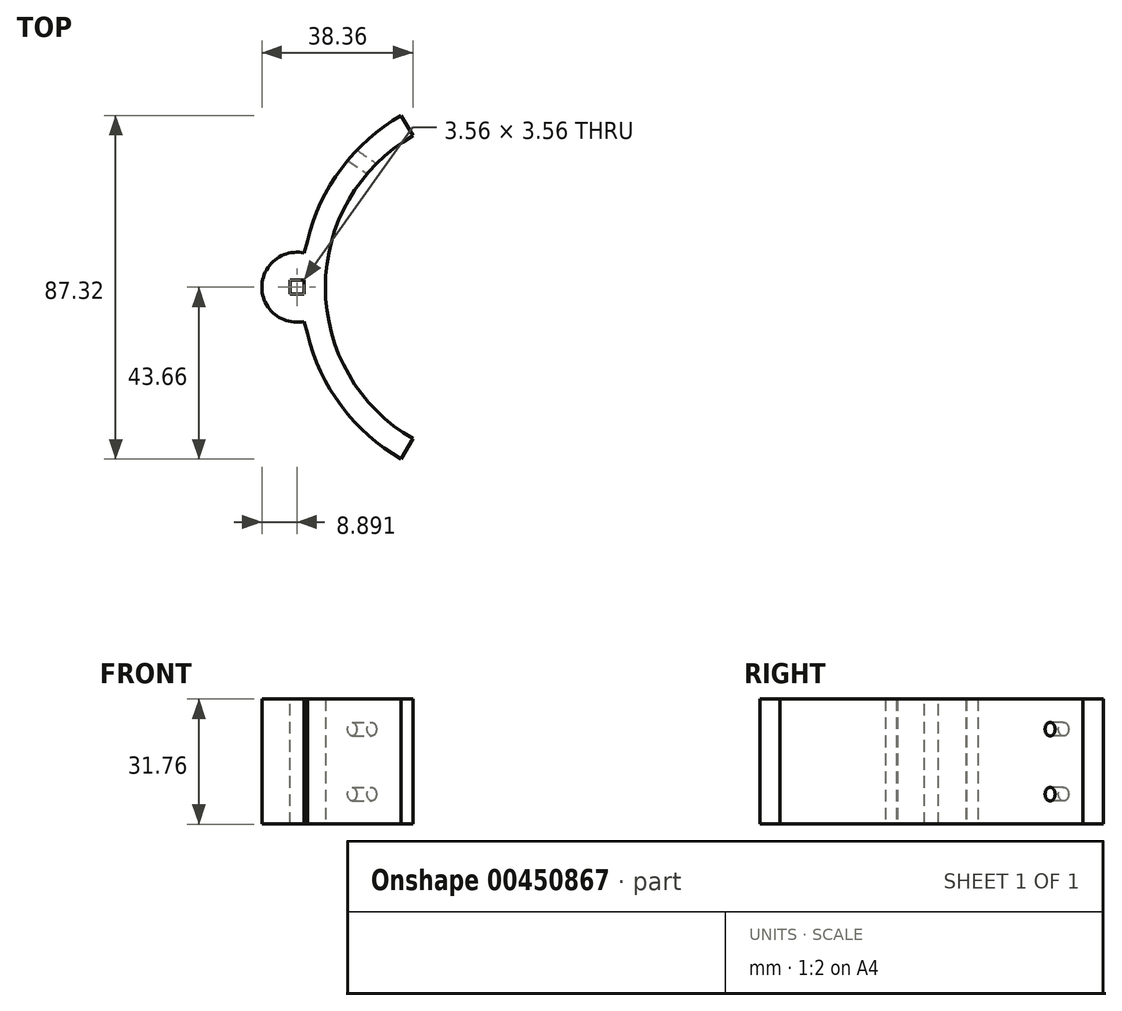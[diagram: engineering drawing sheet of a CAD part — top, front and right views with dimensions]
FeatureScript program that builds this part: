
annotation { "Feature Type Name" : "Feature", "Feature Type Description" : "" }
export const myFeature = defineFeature(function(context is Context, id is Id, definition is map)
    precondition{}
    {
        {
            var Q0;
            Q0=qCreatedBy(makeId("Top.planeOp"),FACE);
            var sketch = newSketch(context, id + "F0", { "sketchPlane" : qUnion([Q0])});
            skArc(sketch, "E0", {"start": v(-22.22, 38.5) * mm, "mid": v(-44.45, 0) * mm, "end": v(-22.22, -38.5) * mm});
            skLineSegment(sketch, "E1", {"start": v(-44.45, 0) * mm, "end": v(-22.23, 0) * mm, "construction": true});
            skPoint(sketch, "E2.start.orphan", {"position": v(-22.23, 0) * mm});
            skArc(sketch, "E3.0", {"start": v(-25.2, 43.66) * mm, "mid": v(-40.4, 30.16) * mm, "end": v(-49.03, 11.75) * mm});
            skLineSegment(sketch, "E4", {"start": v(-25.2, 43.66) * mm, "end": v(-22.22, 38.5) * mm});
            skLineSegment(sketch, "E5", {"start": v(-22.23, -38.5) * mm, "end": v(-25.2, -43.66) * mm});
            skCircle(sketch, "E6", {"center": v(-51.69, 0) * mm, "radius": 1.27 * mm});
            skPoint(sketch, "E6.centerSnap0", {"position": v(-50.42, 0) * mm});
            skLineSegment(sketch, "E7", {"start": v(-49.8, 8.69) * mm, "end": v(-49.03, 11.75) * mm});
            skLineSegment(sketch, "E8", {"start": v(-49.8, -8.69) * mm, "end": v(-49.03, -11.75) * mm});
            skArc(sketch, "E9.trimOffspring", {"start": v(-49.03, -11.75) * mm, "mid": v(-40.4, -30.16) * mm, "end": v(-25.2, -43.66) * mm});
            skArc(sketch, "E10.0", {"start": v(-49.8, 8.69) * mm, "mid": v(-60.58, 0) * mm, "end": v(-49.8, -8.69) * mm});
            skPoint(sketch, "E11.orphan", {"position": v(-51.69, 1.27) * mm});
            skPoint(sketch, "E12.orphan", {"position": v(-51.69, -1.27) * mm});
            skSolve(sketch);
        }
        {
            var Q0;
            Q0=makeQuery(id+"F0.imprint","IMPRINT",FACE,{"disambiguationData":[TD([[makeQuery(id+"F0.imprint","IMPRINT",EDGE,{"derivedFrom":sQuery(id+"F0.wireOp",EDGE,"E0")}),-1.0]])]});
            extrude(context, id + "F1", {"entities" : qUnion([Q0]), "endBound" : BoundingType.SYMMETRIC, "depth" : 31.75 * mm});
        }
        {
            var Q0;
            Q0=makeQuery(id+"F1.opExtrude","CAP_FACE",FACE,{"disambiguationData":[OSD([sQuery(id+"F0.wireOp",EDGE,"E0"),sQuery(id+"F0.wireOp",EDGE,"E3.0"),sQuery(id+"F0.wireOp",EDGE,"E4"),sQuery(id+"F0.wireOp",EDGE,"E5"),sQuery(id+"F0.wireOp",EDGE,"E6"),sQuery(id+"F0.wireOp",EDGE,"E7"),sQuery(id+"F0.wireOp",EDGE,"E8"),sQuery(id+"F0.wireOp",EDGE,"E9.trimOffspring"),sQuery(id+"F0.wireOp",EDGE,"E10.0")])],"isStart":false});
            var sketch = newSketch(context, id + "F2", { "sketchPlane" : qUnion([Q0])});
            skLineSegment(sketch, "E13.bottom", {"start": v(-49.91, -1.78) * mm, "end": v(-53.47, -1.78) * mm});
            skLineSegment(sketch, "E13.top", {"start": v(-49.91, 1.78) * mm, "end": v(-53.47, 1.78) * mm});
            skLineSegment(sketch, "E13.left", {"start": v(-49.91, -1.78) * mm, "end": v(-49.91, 1.78) * mm});
            skLineSegment(sketch, "E13.right", {"start": v(-53.47, -1.78) * mm, "end": v(-53.47, 1.78) * mm});
            skPoint(sketch, "E13.middle", {"position": v(-51.69, 0) * mm});
            skSolve(sketch);
        }
        {
            var Q0;
            Q0=qSketchRegion(id+"F2",true);
            extrude(context, id + "F3", {"entities" : qUnion([Q0]), "operationType" : NewBodyOperationType.REMOVE, "endBound" : BoundingType.THROUGH_ALL, "oppositeDirection" : true, "depth" : 25.4 * mm});
        }
        {
            var Q0;
            Q0=makeQuery(id+"F1.opExtrude","SWEPT_EDGE",EDGE,{"disambiguationData":[OSD([sQuery(id+"F0.wireOp",EDGE,"E0"),sQuery(id+"F0.wireOp",EDGE,"E4")])]});
            var Q1;
            Q1=makeQuery(id+"F3.boolean.opBoolean","INTERSECT",VERTEX,{"derivedFrom":[makeQuery(id+"F1.opExtrude","CAP_FACE",FACE,{"disambiguationData":[OSD([sQuery(id+"F0.wireOp",EDGE,"E0"),sQuery(id+"F0.wireOp",EDGE,"E3.0"),sQuery(id+"F0.wireOp",EDGE,"E4"),sQuery(id+"F0.wireOp",EDGE,"E5"),sQuery(id+"F0.wireOp",EDGE,"E6"),sQuery(id+"F0.wireOp",EDGE,"E7"),sQuery(id+"F0.wireOp",EDGE,"E8"),sQuery(id+"F0.wireOp",EDGE,"E9.trimOffspring"),sQuery(id+"F0.wireOp",EDGE,"E10.0")])],"isStart":true}),makeQuery(id+"F3.opExtrude","SWEPT_FACE",FACE,{"disambiguationData":[OSD([sQuery(id+"F2.wireOp",EDGE,"E13.bottom")])]}),makeQuery(id+"F3.opExtrude","SWEPT_FACE",FACE,{"disambiguationData":[OSD([sQuery(id+"F2.wireOp",EDGE,"E13.left")])]})]});
            cPlane(context, id + "F4", {"entities" : qUnion([Q0, Q1]), "cplaneType" : CPlaneType.LINE_ANGLE, "offset" : 25.4 * mm, "angle" : 0 * degree, "width" : 152.4 * mm, "height" : 152.4 * mm});
        }
        {
            var Q0;
            Q0=qCreatedBy(id+"F4.planeOp",FACE);
            var sketch = newSketch(context, id + "F5", { "sketchPlane" : qUnion([Q0])});
            skPoint(sketch, "E14", {"position": v(-6.31, 8.26) * mm});
            skPoint(sketch, "E15", {"position": v(-6.31, -8.26) * mm});
            skPoint(sketch, "E16", {"position": v(-6.31, 15.88) * mm});
            skPoint(sketch, "E17", {"position": v(-6.31, -15.88) * mm});
            skPoint(sketch, "E18", {"position": v(-19.01, 15.88) * mm});
            skPoint(sketch, "E19", {"position": v(-19.01, -15.87) * mm});
            skSolve(sketch);
        }
        {
            var Q0;
            Q0=sQuery(id+"F5.wireOp",VERTEX,"E14");
            var Q1;
            Q1=sQuery(id+"F5.wireOp",VERTEX,"E15");
            var Q2;
            Q2=makeQuery(id+"F1.opExtrude","SWEPT_BODY",BODY,{"disambiguationData":[OSD([sQuery(id+"F0.wireOp",EDGE,"E0"),sQuery(id+"F0.wireOp",EDGE,"E3.0"),sQuery(id+"F0.wireOp",EDGE,"E4"),sQuery(id+"F0.wireOp",EDGE,"E5"),sQuery(id+"F0.wireOp",EDGE,"E6"),sQuery(id+"F0.wireOp",EDGE,"E7"),sQuery(id+"F0.wireOp",EDGE,"E8"),sQuery(id+"F0.wireOp",EDGE,"E9.trimOffspring"),sQuery(id+"F0.wireOp",EDGE,"E10.0")])]});
            hole(context, id + "F6", {"style" : HoleStyle.SIMPLE, "endStyle" : HoleEndStyle.THROUGH, "oppositeDirection" : true, "holeDiameter" : 3.45 * mm, "isTappedThrough" : true, "tappedDepth" : 12.7 * mm, "tapClearance" : 3, "locations" : qUnion([Q0, Q1]), "scope" : qUnion([Q2])});
        }
    });
